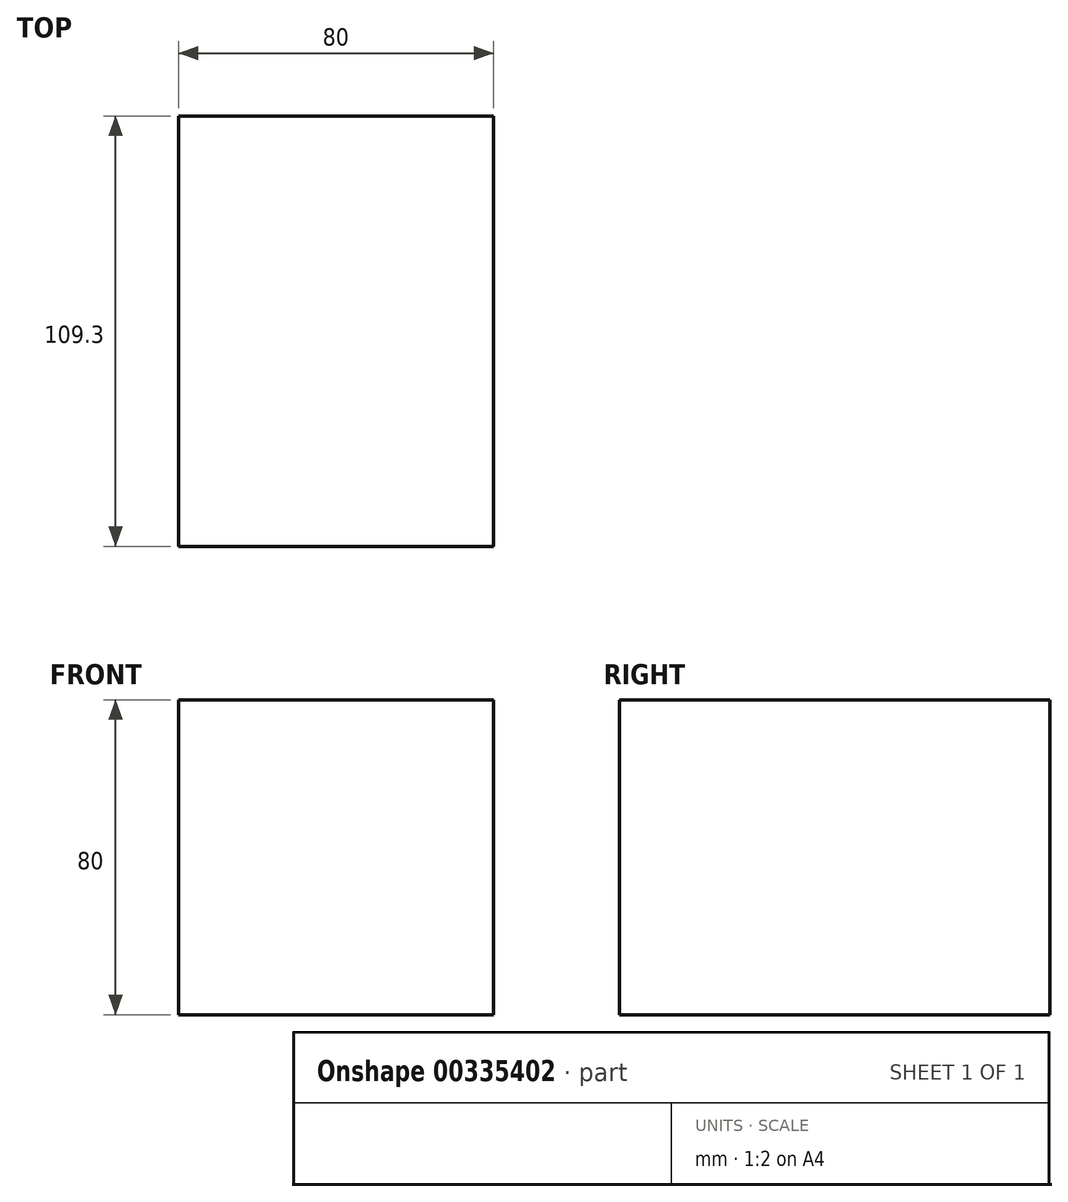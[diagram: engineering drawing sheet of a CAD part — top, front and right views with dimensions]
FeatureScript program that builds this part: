
annotation { "Feature Type Name" : "Feature", "Feature Type Description" : "" }
export const myFeature = defineFeature(function(context is Context, id is Id, definition is map)
    precondition{}
    {
        {
            var Q0;
            Q0=qCreatedBy(makeId("Top.planeOp"),FACE);
            var sketch = newSketch(context, id + "F0", { "sketchPlane" : qUnion([Q0])});
            skLineSegment(sketch, "E0.bottom", {"start": v(-40, 54.65) * mm, "end": v(40, 54.65) * mm});
            skLineSegment(sketch, "E0.top", {"start": v(-40, -54.65) * mm, "end": v(40, -54.65) * mm});
            skLineSegment(sketch, "E0.left", {"start": v(-40, 54.65) * mm, "end": v(-40, -54.65) * mm});
            skLineSegment(sketch, "E0.right", {"start": v(40, 54.65) * mm, "end": v(40, -54.65) * mm});
            skPoint(sketch, "E0.middle", {"position": v(0, 0) * mm});
            skSolve(sketch);
        }
        {
            var Q0;
            Q0=makeQuery(id+"F0.imprint","IMPRINT",FACE,{"disambiguationData":[TD([[makeQuery(id+"F0.imprint","IMPRINT",EDGE,{"derivedFrom":sQuery(id+"F0.wireOp",EDGE,"E0.bottom")}),-1.0]])]});
            extrude(context, id + "F1", {"entities" : qUnion([Q0]), "endBound" : BoundingType.SYMMETRIC, "depth" : 80 * mm});
        }
    });
